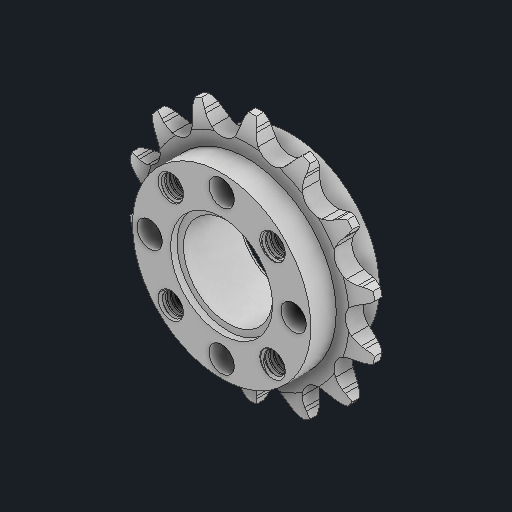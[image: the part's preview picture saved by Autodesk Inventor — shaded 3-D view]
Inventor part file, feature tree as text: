
AUTODESK INVENTOR PART (.ipt)
format: ipt  version: 2023 (Build 270158000, 158)  size: 2,117,632 bytes
history: native  units: in
note: dims shown in document units (in); Inventor stores cm internally (conversion verified against a paired STEP export)
features: mirror x1
ambient origin geometry x8: Origin, YZ Plane, XZ Plane, XY Plane, X Axis, Y Axis, Z Axis, Center Point
bodies: Solid1 (feature_tree)
feature tree (1):
  mirror  "Mirror4"
